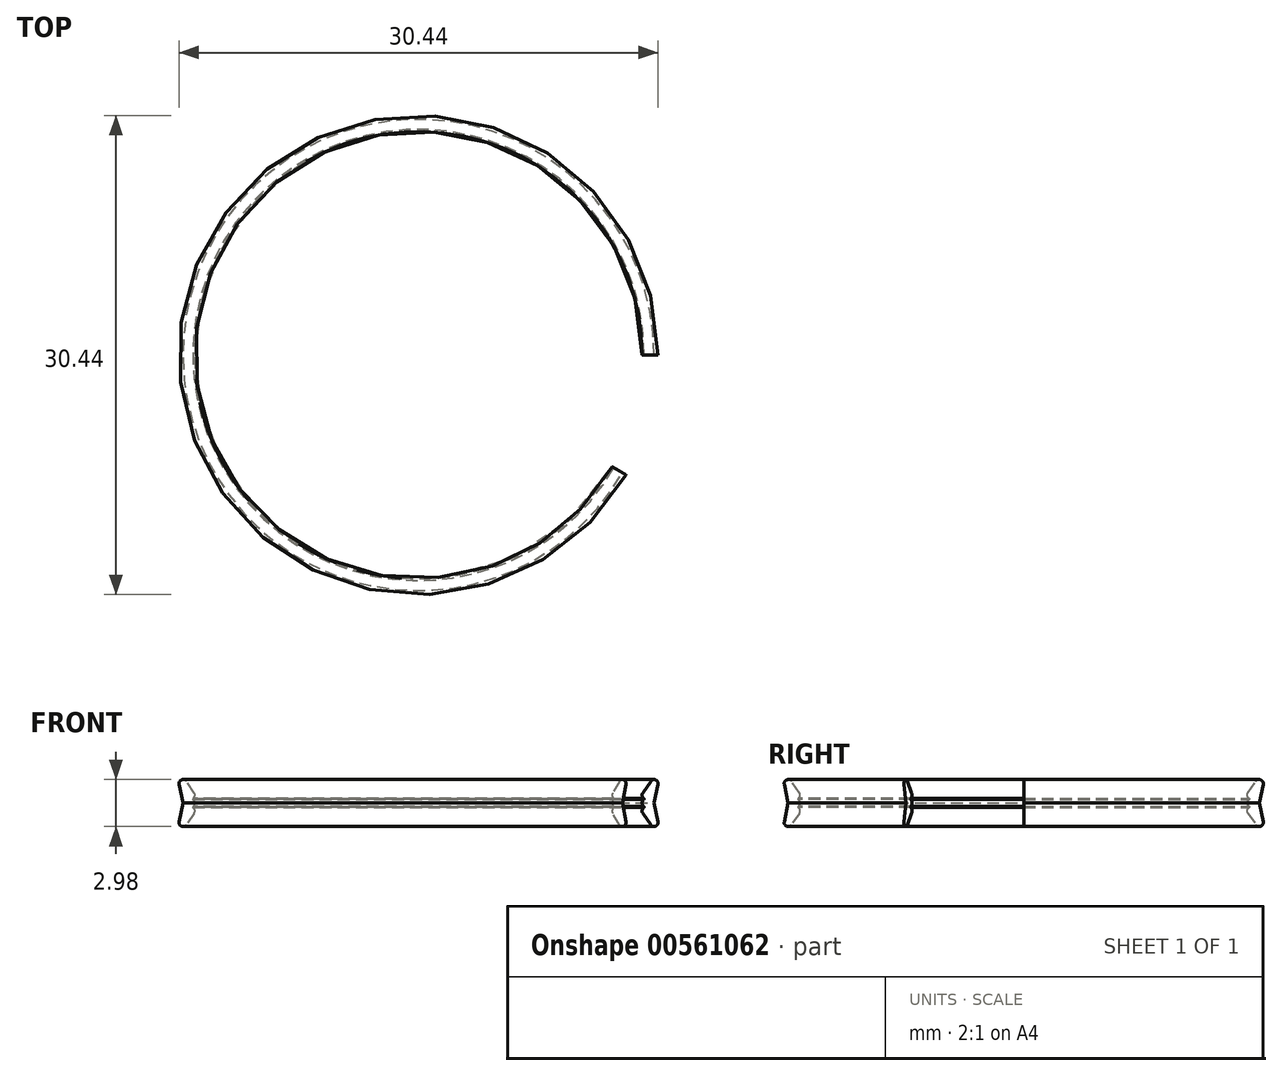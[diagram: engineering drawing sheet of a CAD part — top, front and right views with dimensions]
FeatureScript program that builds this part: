
annotation { "Feature Type Name" : "Feature", "Feature Type Description" : "" }
export const myFeature = defineFeature(function(context is Context, id is Id, definition is map)
    precondition{}
    {
        {
            var Q0;
            Q0=qCreatedBy(makeId("Front.planeOp"),FACE);
            var sketch = newSketch(context, id + "F0", { "sketchPlane" : qUnion([Q0])});
            skLineSegment(sketch, "E0", {"start": v(0, 0) * mm, "end": v(0, 3.94) * mm, "construction": true});
            skLineSegment(sketch, "E1", {"start": v(14.36, 2.03) * mm, "end": v(14.36, 0) * mm, "construction": true});
            skLineSegment(sketch, "E2", {"start": v(14.36, 0) * mm, "end": v(7.64, 0) * mm, "construction": true});
            skLineSegment(sketch, "E3", {"start": v(14.36, 2.03) * mm, "end": v(15.38, 2.03) * mm, "construction": true});
            skLineSegment(sketch, "E4", {"start": v(15.38, 2.03) * mm, "end": v(15.38, 0) * mm, "construction": true});
            skLineSegment(sketch, "E5", {"start": v(15.38, 0) * mm, "end": v(15.5, 0) * mm, "construction": true});
            skLineSegment(sketch, "E6", {"start": v(15.5, 0) * mm, "end": v(16, 0.5) * mm, "construction": true});
            skLineSegment(sketch, "E7", {"start": v(16, 0.5) * mm, "end": v(16, 4.02) * mm, "construction": true});
            skLineSegment(sketch, "E8", {"start": v(14.2, 0.54) * mm, "end": v(14.96, 0.54) * mm});
            skLineSegment(sketch, "E9", {"start": v(14.96, 0.54) * mm, "end": v(15.21, 1.73) * mm});
            skLineSegment(sketch, "E10", {"start": v(14.75, 1.92) * mm, "end": v(14.25, 1.2) * mm});
            skArc(sketch, "E11", {"start": v(14.25, 1.2) * mm, "mid": v(14.2, 1) * mm, "end": v(14.33, 0.83) * mm});
            skLineSegment(sketch, "E12", {"start": v(14.2, 1.05) * mm, "end": v(14.2, 0.37) * mm, "construction": true});
            skLineSegment(sketch, "E13", {"start": v(14.33, 0.83) * mm, "end": v(14.33, 0.76) * mm});
            skArc(sketch, "E14", {"start": v(14.33, 0.76) * mm, "mid": v(14.23, 0.67) * mm, "end": v(14.2, 0.54) * mm});
            skPoint(sketch, "E15.visualSharp", {"position": v(15.47, 2.95) * mm});
            skArc(sketch, "E15.filletArc", {"start": v(15.21, 1.73) * mm, "mid": v(15.06, 2.01) * mm, "end": v(14.75, 1.92) * mm});
            skArc(sketch, "E16.MirrorCS", {"start": v(14.33, 0.32) * mm, "mid": v(14.23, 0.41) * mm, "end": v(14.2, 0.54) * mm});
            skLineSegment(sketch, "E17.MirrorCS", {"start": v(14.33, 0.25) * mm, "end": v(14.33, 0.32) * mm});
            skArc(sketch, "E18.MirrorCS", {"start": v(14.25, -0.11) * mm, "mid": v(14.2, 0.09) * mm, "end": v(14.33, 0.25) * mm});
            skLineSegment(sketch, "E19.MirrorCS", {"start": v(14.75, -0.84) * mm, "end": v(14.25, -0.11) * mm});
            skArc(sketch, "E20.MirrorCS", {"start": v(15.21, -0.64) * mm, "mid": v(15.06, -0.93) * mm, "end": v(14.75, -0.84) * mm});
            skLineSegment(sketch, "E21.MirrorCS", {"start": v(14.96, 0.54) * mm, "end": v(15.21, -0.64) * mm});
            skSolve(sketch);
        }
        {
            var Q0;
            Q0=makeQuery(id+"F0.imprint","IMPRINT",FACE,{"disambiguationData":[TD([[makeQuery(id+"F0.imprint","IMPRINT",EDGE,{"derivedFrom":sQuery(id+"F0.wireOp",EDGE,"E8")}),1.0]])]});
            var Q1;
            Q1=makeQuery(id+"F0.imprint","IMPRINT",FACE,{"disambiguationData":[TD([[makeQuery(id+"F0.imprint","IMPRINT",EDGE,{"derivedFrom":sQuery(id+"F0.wireOp",EDGE,"E8")}),-1.0]])]});
            var Q2;
            Q2=sQuery(id+"F0.wireOp",EDGE,"E0");
            revolve(context, id + "F1", {"entities" : qUnion([Q0, Q1]), "axis" : qUnion([Q2]), "revolveType" : RevolveType.ONE_DIRECTION, "angle" : 330 * degree});
        }
    });
